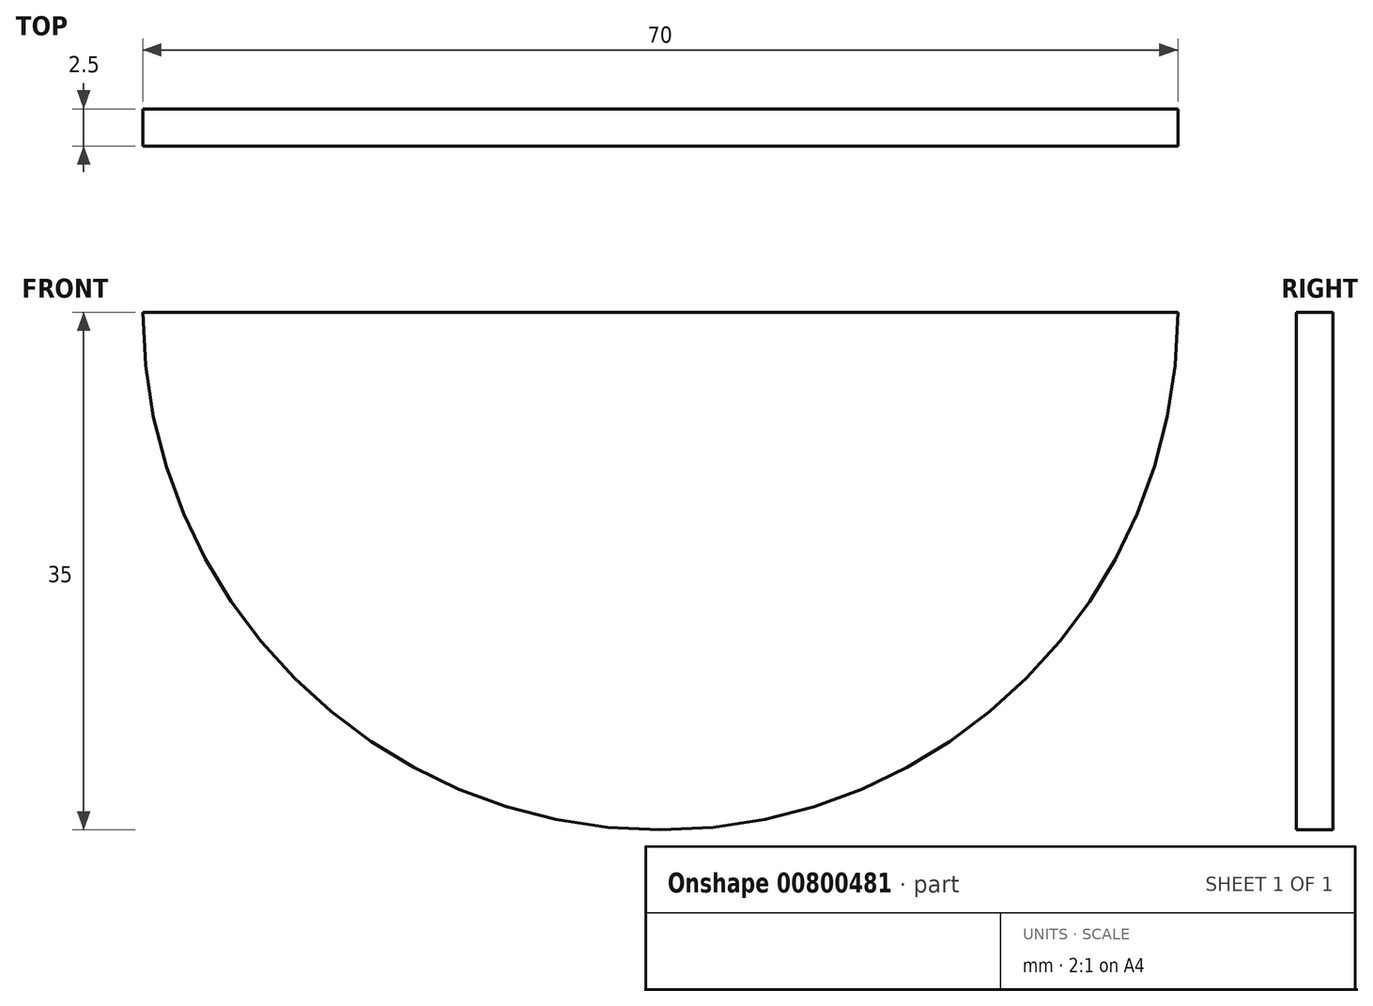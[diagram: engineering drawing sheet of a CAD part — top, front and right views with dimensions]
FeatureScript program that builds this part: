
annotation { "Feature Type Name" : "Feature", "Feature Type Description" : "" }
export const myFeature = defineFeature(function(context is Context, id is Id, definition is map)
    precondition{}
    {
        {
            var Q0;
            Q0=qCreatedBy(makeId("Front.planeOp"),FACE);
            var sketch = newSketch(context, id + "F0", { "sketchPlane" : qUnion([Q0])});
            skLineSegment(sketch, "E0", {"start": v(0, 0) * mm, "end": v(-35, 0) * mm});
            skArc(sketch, "E1", {"start": v(-35, 0) * mm, "mid": v(-24.75, -24.75) * mm, "end": v(0, -35) * mm});
            skArc(sketch, "E2.MirrorCS", {"start": v(35, 0) * mm, "mid": v(24.75, -24.75) * mm, "end": v(0, -35) * mm});
            skLineSegment(sketch, "E3.MirrorCS", {"start": v(0, 0) * mm, "end": v(35, 0) * mm});
            skSolve(sketch);
        }
        {
            var Q0;
            Q0=makeQuery(id+"F0.imprint","IMPRINT",FACE,{"disambiguationData":[TD([[makeQuery(id+"F0.imprint","IMPRINT",EDGE,{"derivedFrom":sQuery(id+"F0.wireOp",EDGE,"E0")}),1.0]])]});
            extrude(context, id + "F1", {"entities" : qUnion([Q0]), "depth" : 2.5 * mm, "offsetDistance" : 25 * mm});
        }
    });
